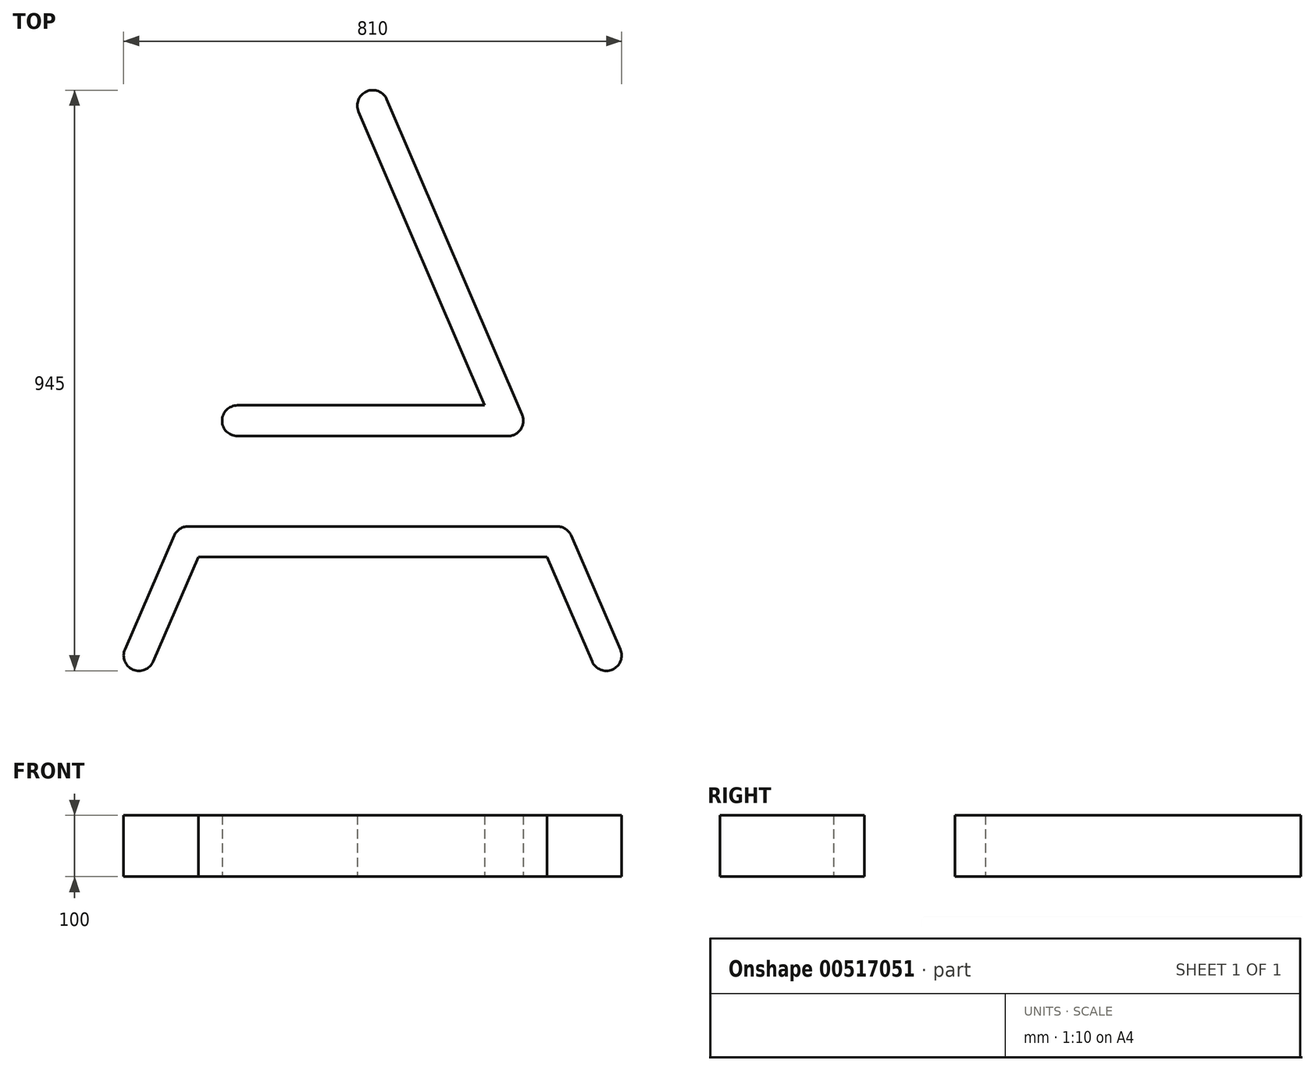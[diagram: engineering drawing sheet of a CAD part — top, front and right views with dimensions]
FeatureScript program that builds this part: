
annotation { "Feature Type Name" : "Feature", "Feature Type Description" : "" }
export const myFeature = defineFeature(function(context is Context, id is Id, definition is map)
    precondition{}
    {
        {
            var Q0;
            Q0=qCreatedBy(makeId("Top.planeOp"),FACE);
            var sketch = newSketch(context, id + "F0", { "sketchPlane" : qUnion([Q0])});
            skCircle(sketch, "E0", {"center": v(0, 448) * mm, "radius": 25 * mm});
            skCircle(sketch, "E1", {"center": v(220, -65) * mm, "radius": 25 * mm});
            skCircle(sketch, "E2", {"center": v(-220, -65) * mm, "radius": 25 * mm});
            skCircle(sketch, "E3", {"center": v(-300, -262) * mm, "radius": 25 * mm});
            skCircle(sketch, "E4", {"center": v(300, -262) * mm, "radius": 25 * mm});
            skCircle(sketch, "E5", {"center": v(380, -447) * mm, "radius": 25 * mm});
            skCircle(sketch, "E6", {"center": v(-380, -447) * mm, "radius": 25 * mm});
            skLineSegment(sketch, "E7", {"start": v(22.98, 457.85) * mm, "end": v(242.98, -55.15) * mm});
            skLineSegment(sketch, "E8", {"start": v(-22.98, 438.15) * mm, "end": v(197.02, -74.85) * mm});
            skLineSegment(sketch, "E9", {"start": v(220, -90) * mm, "end": v(-220, -90) * mm});
            skLineSegment(sketch, "E10", {"start": v(220, -40) * mm, "end": v(-220, -40) * mm});
            skLineSegment(sketch, "E11", {"start": v(-300, -237) * mm, "end": v(300, -237) * mm});
            skLineSegment(sketch, "E12", {"start": v(-300, -287) * mm, "end": v(300, -287) * mm});
            skLineSegment(sketch, "E13", {"start": v(-322.95, -252.08) * mm, "end": v(-402.95, -437.08) * mm});
            skLineSegment(sketch, "E14", {"start": v(-357.05, -456.92) * mm, "end": v(-277.05, -271.92) * mm});
            skLineSegment(sketch, "E15", {"start": v(322.95, -252.08) * mm, "end": v(402.95, -437.08) * mm});
            skLineSegment(sketch, "E16", {"start": v(277.05, -271.92) * mm, "end": v(357.05, -456.92) * mm});
            skSolve(sketch);
        }
        {
            var Q0;
            Q0 = qSketchRegion(id + "F0", true);
            extrude(context, id + "F1", {"entities" : qUnion([Q0]), "depth" : 100 * mm, "offsetDistance" : 25 * mm});
        }
    });
